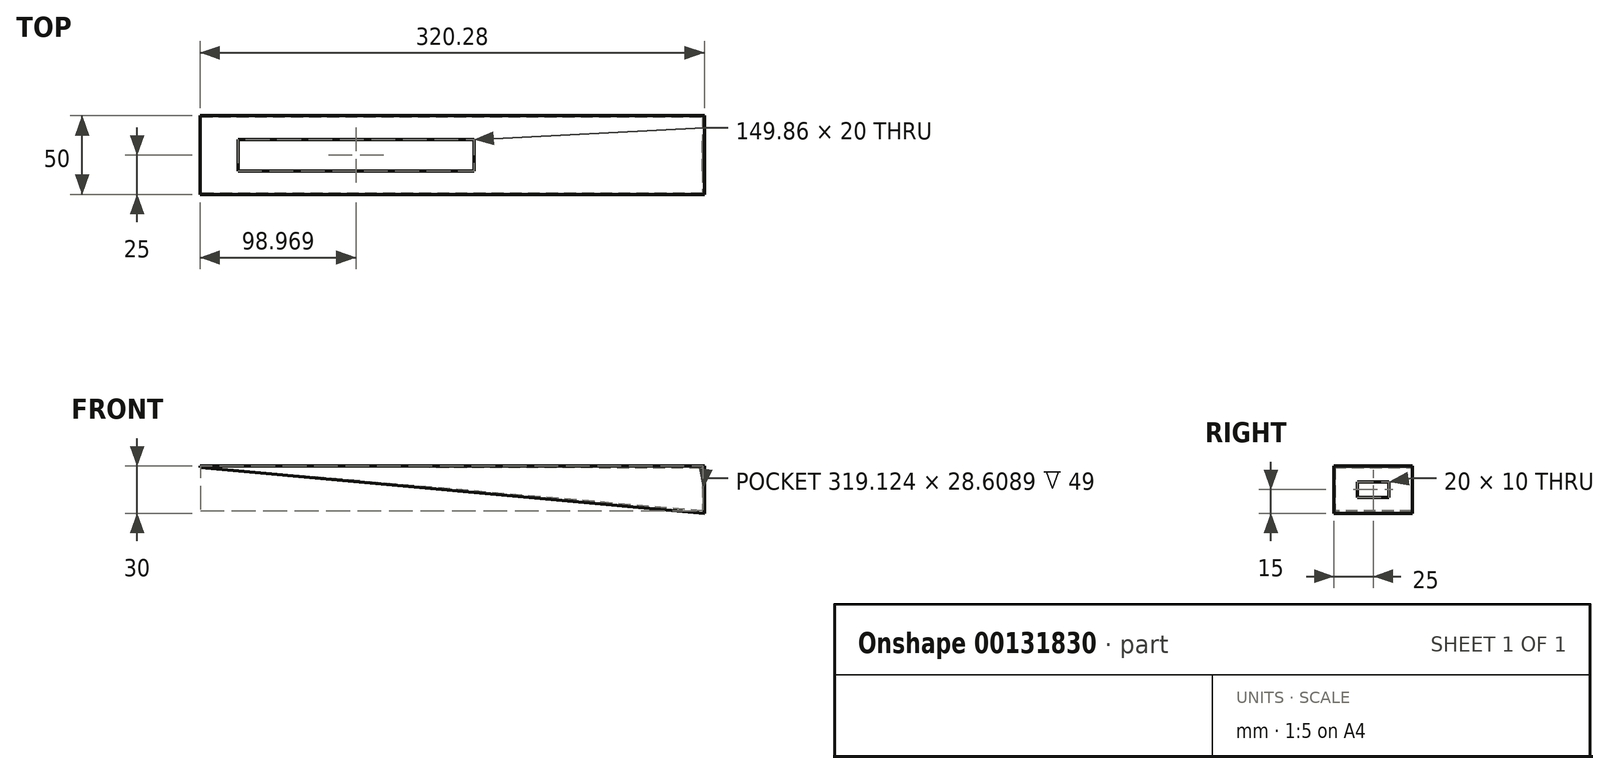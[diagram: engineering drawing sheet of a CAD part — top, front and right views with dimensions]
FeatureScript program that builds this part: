
annotation { "Feature Type Name" : "Feature", "Feature Type Description" : "" }
export const myFeature = defineFeature(function(context is Context, id is Id, definition is map)
    precondition{}
    {
        {
            var Q0;
            Q0=qCreatedBy(makeId("Front.planeOp"),FACE);
            var sketch = newSketch(context, id + "F0", { "sketchPlane" : qUnion([Q0])});
            skLineSegment(sketch, "E0", {"start": v(-69.66, 0) * mm, "end": v(250.34, 0) * mm});
            skLineSegment(sketch, "E1", {"start": v(-69.8, -0.9) * mm, "end": v(250.34, -30) * mm});
            skLineSegment(sketch, "E2", {"start": v(250.34, -30) * mm, "end": v(250.34, 0) * mm});
            skLineSegment(sketch, "E3", {"start": v(-69.66, -0.03) * mm, "end": v(249.33, -0.97) * mm});
            skLineSegment(sketch, "E4", {"start": v(249.33, -0.97) * mm, "end": v(249.25, -28.64) * mm});
            skLineSegment(sketch, "E5", {"start": v(249.25, -28.64) * mm, "end": v(-69.79, -0.83) * mm});
            skLineSegment(sketch, "E6", {"start": v(-69.66, -0.03) * mm, "end": v(-69.79, -0.83) * mm});
            skLineSegment(sketch, "E7", {"start": v(-69.94, -0.88) * mm, "end": v(-69.8, -0.9) * mm});
            skLineSegment(sketch, "E8", {"start": v(-69.8, 0) * mm, "end": v(-69.94, -0.88) * mm});
            skLineSegment(sketch, "E9", {"start": v(-69.8, 0) * mm, "end": v(-69.66, 0) * mm});
            skSolve(sketch);
        }
        {
            var Q0;
            Q0=makeQuery(id+"F0.imprint","IMPRINT",FACE,{"disambiguationData":[TD([[makeQuery(id+"F0.imprint","IMPRINT",EDGE,{"derivedFrom":sQuery(id+"F0.wireOp",EDGE,"hZ2UMt2E-fBOG-nuDn-IccN-yUAMeZouQCkQ")}),-1.0]])]});
            var Q1;
            Q1=makeQuery(id+"F0.imprint","IMPRINT",FACE,{"disambiguationData":[TD([[makeQuery(id+"F0.imprint","IMPRINT",EDGE,{"derivedFrom":sQuery(id+"F0.wireOp",EDGE,"E0")}),-1.0]])]});
            var Q2;
            Q2=makeQuery(id+"F0.imprint","IMPRINT",FACE,{"disambiguationData":[TD([[makeQuery(id+"F0.imprint","IMPRINT",EDGE,{"derivedFrom":sQuery(id+"F0.wireOp",EDGE,"E3")}),-1.0]])]});
            extrude(context, id + "F1", {"entities" : qUnion([Q0, Q1, Q2]), "depth" : 50 * mm, "symmetric" : true});
        }
        {
            var Q0;
            Q0=makeQuery(id+"F0.imprint","IMPRINT",FACE,{"disambiguationData":[TD([[makeQuery(id+"F0.imprint","IMPRINT",EDGE,{"derivedFrom":sQuery(id+"F0.wireOp",EDGE,"E3")}),-1.0]])]});
            extrude(context, id + "F2", {"entities" : qUnion([Q0]), "operationType" : NewBodyOperationType.REMOVE, "oppositeDirection" : true, "depth" : 49 * mm, "symmetric" : true});
        }
        {
            var Q0;
            Q0=makeQuery(id+"F1.opExtrude","SWEPT_FACE",FACE,{"disambiguationData":[OSD([sQuery(id+"F0.wireOp",EDGE,"E2")])]});
            var sketch = newSketch(context, id + "F3", { "sketchPlane" : qUnion([Q0])});
            skLineSegment(sketch, "E10.bottom", {"start": v(-10, -10) * mm, "end": v(10, -10) * mm});
            skLineSegment(sketch, "E10.top", {"start": v(-10, -20) * mm, "end": v(10, -20) * mm});
            skLineSegment(sketch, "E10.left", {"start": v(-10, -10) * mm, "end": v(-10, -20) * mm});
            skLineSegment(sketch, "E10.right", {"start": v(10, -10) * mm, "end": v(10, -20) * mm});
            skSolve(sketch);
        }
        {
            var Q0;
            Q0=makeQuery(id+"F3.imprint","IMPRINT",FACE,{"disambiguationData":[TD([[makeQuery(id+"F3.imprint","IMPRINT",EDGE,{"derivedFrom":sQuery(id+"F3.wireOp",EDGE,"E10.bottom")}),-1.0]])]});
            extrude(context, id + "F4", {"entities" : qUnion([Q0]), "operationType" : NewBodyOperationType.REMOVE, "endBound" : BoundingType.UP_TO_NEXT, "oppositeDirection" : true, "depth" : 25 * mm});
        }
        {
            var Q0;
            Q0=makeQuery(id+"F1.opExtrude","SWEPT_FACE",FACE,{"disambiguationData":[OSD([sQuery(id+"F0.wireOp",EDGE,"E0"),sQuery(id+"F0.wireOp",EDGE,"E9")])]});
            var sketch = newSketch(context, id + "F5", { "sketchPlane" : qUnion([Q0])});
            skLineSegment(sketch, "E11.bottom", {"start": v(-45.9, 10) * mm, "end": v(103.96, 10) * mm});
            skLineSegment(sketch, "E11.top", {"start": v(-45.9, -10) * mm, "end": v(103.96, -10) * mm});
            skLineSegment(sketch, "E11.left", {"start": v(-45.9, 10) * mm, "end": v(-45.9, -10) * mm});
            skLineSegment(sketch, "E11.right", {"start": v(103.96, 10) * mm, "end": v(103.96, -10) * mm});
            skSolve(sketch);
        }
        {
            var Q0;
            Q0=makeQuery(id+"F5.imprint","IMPRINT",FACE,{"disambiguationData":[TD([[makeQuery(id+"F5.imprint","IMPRINT",EDGE,{"derivedFrom":sQuery(id+"F5.wireOp",EDGE,"E11.bottom")}),-1.0]])]});
            extrude(context, id + "F6", {"entities" : qUnion([Q0]), "operationType" : NewBodyOperationType.REMOVE, "endBound" : BoundingType.UP_TO_NEXT, "oppositeDirection" : true, "depth" : 25 * mm});
        }
    });
